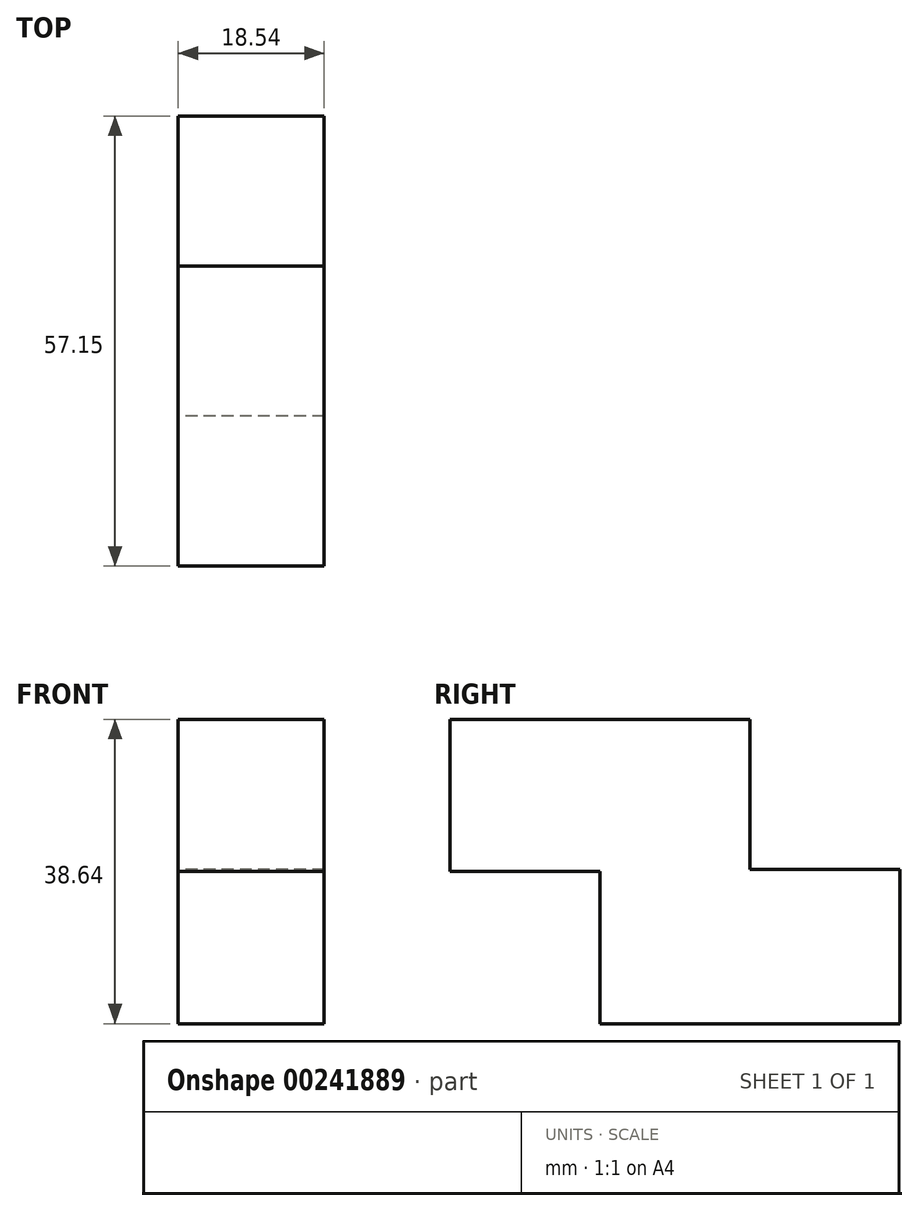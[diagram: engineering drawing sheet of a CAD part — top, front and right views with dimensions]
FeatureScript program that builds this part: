
annotation { "Feature Type Name" : "Feature", "Feature Type Description" : "" }
export const myFeature = defineFeature(function(context is Context, id is Id, definition is map)
    precondition{}
    {
        {
            var Q0;
            Q0=qCreatedBy(makeId("Front.planeOp"),FACE);
            var sketch = newSketch(context, id + "F0", { "sketchPlane" : qUnion([Q0])});
            skLineSegment(sketch, "E0.bottom", {"start": v(-39.8, 40.28) * mm, "end": v(-21.26, 40.28) * mm});
            skLineSegment(sketch, "E0.top", {"start": v(-39.8, 20.69) * mm, "end": v(-21.26, 20.69) * mm});
            skLineSegment(sketch, "E0.left", {"start": v(-39.8, 40.28) * mm, "end": v(-39.8, 20.69) * mm});
            skLineSegment(sketch, "E0.right", {"start": v(-21.26, 40.28) * mm, "end": v(-21.26, 20.69) * mm});
            skSolve(sketch);
        }
        {
            var Q0;
            Q0=makeQuery(id+"F0.imprint","IMPRINT",FACE,{"disambiguationData":[TD([[makeQuery(id+"F0.imprint","IMPRINT",EDGE,{"derivedFrom":sQuery(id+"F0.wireOp",EDGE,"E0.bottom")}),-1.0]])]});
            extrude(context, id + "F1", {"entities" : qUnion([Q0]), "oppositeDirection" : true, "depth" : 38.1 * mm});
        }
        {
            var Q0;
            Q0=makeQuery(id+"F1.opExtrude","SWEPT_FACE",FACE,{"disambiguationData":[OSD([sQuery(id+"F0.wireOp",EDGE,"E0.bottom")])]});
            var sketch = newSketch(context, id + "F2", { "sketchPlane" : qUnion([Q0])});
            skLineSegment(sketch, "E1.bottom", {"start": v(-21.26, 0) * mm, "end": v(-39.8, 0) * mm});
            skLineSegment(sketch, "E1.top", {"start": v(-21.26, 19.05) * mm, "end": v(-39.8, 19.05) * mm});
            skLineSegment(sketch, "E1.left", {"start": v(-21.26, 0) * mm, "end": v(-21.26, 19.05) * mm});
            skLineSegment(sketch, "E1.right", {"start": v(-39.8, 0) * mm, "end": v(-39.8, 19.05) * mm});
            skSolve(sketch);
        }
        {
            var Q0;
            Q0=makeQuery(id+"F2.imprint","IMPRINT",FACE,{"disambiguationData":[TD([[makeQuery(id+"F2.imprint","IMPRINT",EDGE,{"derivedFrom":sQuery(id+"F2.wireOp",EDGE,"E1.bottom")}),1.0]])]});
            extrude(context, id + "F3", {"entities" : qUnion([Q0]), "operationType" : NewBodyOperationType.ADD, "depth" : 19.05 * mm});
        }
        {
            var Q0;
            Q0=makeQuery(id+"F3.boolean.opBoolean","MERGE",FACE,{"derivedFrom":[makeQuery(id+"F1.opExtrude","CAP_FACE",FACE,{"disambiguationData":[OSD([sQuery(id+"F0.wireOp",EDGE,"E0.bottom"),sQuery(id+"F0.wireOp",EDGE,"E0.top"),sQuery(id+"F0.wireOp",EDGE,"E0.left"),sQuery(id+"F0.wireOp",EDGE,"E0.right")])],"isStart":true}),makeQuery(id+"F3.opExtrude","SWEPT_FACE",FACE,{"disambiguationData":[OSD([sQuery(id+"F2.wireOp",EDGE,"E1.bottom")])]})]});
            var sketch = newSketch(context, id + "F4", { "sketchPlane" : qUnion([Q0])});
            skLineSegment(sketch, "E2.bottom", {"start": v(-21.26, 59.33) * mm, "end": v(-39.8, 59.33) * mm});
            skLineSegment(sketch, "E2.top", {"start": v(-21.26, 40.01) * mm, "end": v(-39.8, 40.01) * mm});
            skLineSegment(sketch, "E2.left", {"start": v(-21.26, 59.33) * mm, "end": v(-21.26, 40.01) * mm});
            skLineSegment(sketch, "E2.right", {"start": v(-39.8, 59.33) * mm, "end": v(-39.8, 40.01) * mm});
            skSolve(sketch);
        }
        {
            var Q0;
            Q0=makeQuery(id+"F4.imprint","IMPRINT",FACE,{"disambiguationData":[TD([[makeQuery(id+"F4.imprint","IMPRINT",EDGE,{"derivedFrom":sQuery(id+"F4.wireOp",EDGE,"E2.bottom")}),-1.0]])]});
            extrude(context, id + "F5", {"entities" : qUnion([Q0]), "operationType" : NewBodyOperationType.ADD, "depth" : 19.05 * mm});
        }
    });
